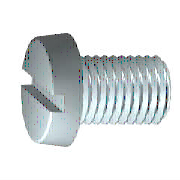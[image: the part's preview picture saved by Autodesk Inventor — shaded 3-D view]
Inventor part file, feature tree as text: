
AUTODESK INVENTOR PART (.ipt)
format: ipt  version: 2023.2 (Build 272271030, 271C)  size: 179,200 bytes
history: native  units: mm (DEFAULTED — no unit token found)
features: sketch x2, extrude x1, plane x1
ambient origin geometry x7: Origin, YZ Plane, XZ Plane, X Axis, Y Axis, Z Axis, Center Point
bodies: Solid1 (feature_tree), Body (feature_tree)
feature tree (4):
  sketch  "Sketch2"  dims[d2=0.49086mm d3=3.3mm d4=5.0mm d5=4.566987mm d8=90.0deg d7=0.0mm d9=8.5mm d10=0.872665mm d11=1.2mm d12=8.5mm d14=0.2mm d15=26.4mm d16=0.0mm d17=0.433015mm d18=0.49086mm d19=1.3mm d20=0.0mm d36=45.0deg d37=0.0mm d39=0.0mm]
  extrude  "Slot"  Depth=26.4mm
  plane  "Work Plane1"
  sketch  "Sketch1"  dims[d0=28.0mm d1=26.4mm]
